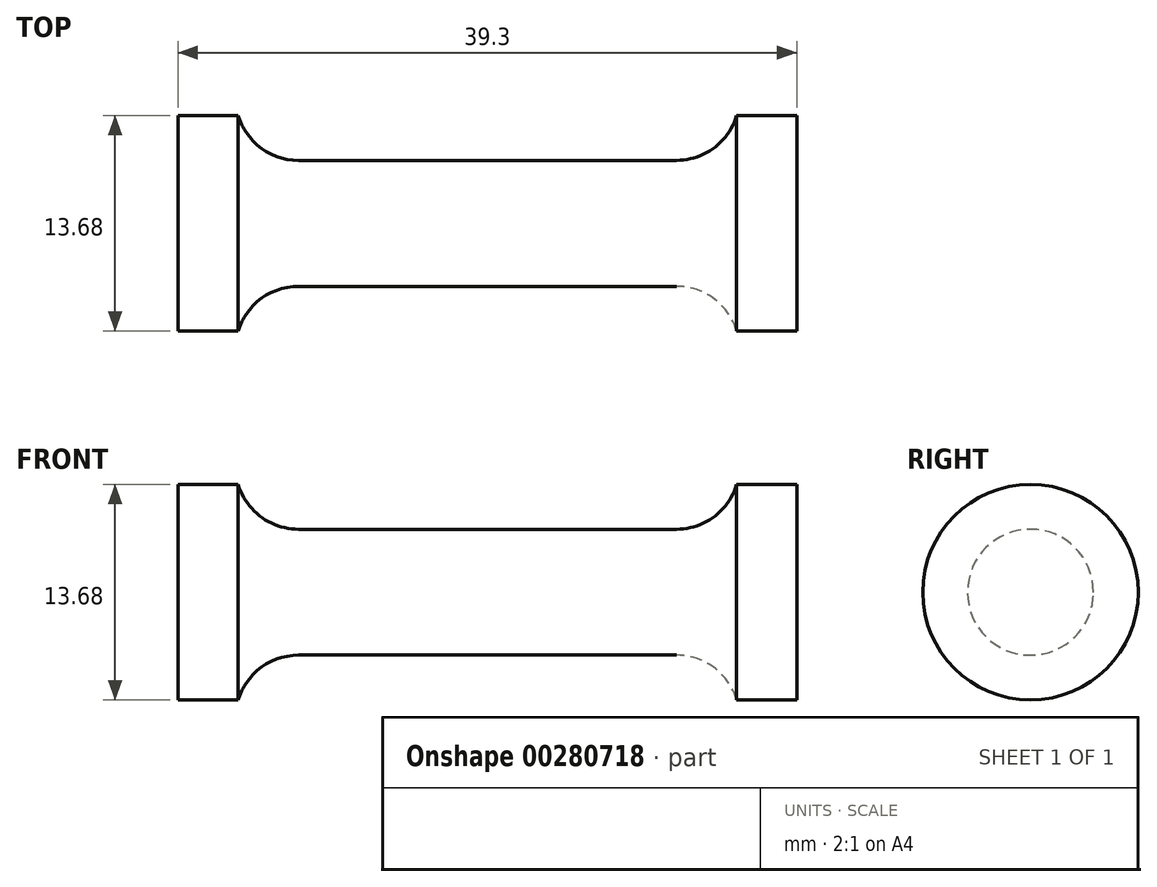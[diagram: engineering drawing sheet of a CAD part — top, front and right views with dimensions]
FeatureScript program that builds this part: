
annotation { "Feature Type Name" : "Feature", "Feature Type Description" : "" }
export const myFeature = defineFeature(function(context is Context, id is Id, definition is map)
    precondition{}
    {
        {
            var Q0;
            Q0=qCreatedBy(makeId("Front.planeOp"),FACE);
            var sketch = newSketch(context, id + "F0", { "sketchPlane" : qUnion([Q0])});
            skLineSegment(sketch, "E0", {"start": v(0, 4) * mm, "end": v(12, 4) * mm});
            skArc(sketch, "E1", {"start": v(12, 4) * mm, "mid": v(14.39, 4.79) * mm, "end": v(15.83, 6.84) * mm});
            skLineSegment(sketch, "E2", {"start": v(15.83, 6.84) * mm, "end": v(19.65, 6.84) * mm});
            skLineSegment(sketch, "E3", {"start": v(19.65, 6.84) * mm, "end": v(19.65, 0) * mm});
            skLineSegment(sketch, "E4.MirrorCS", {"start": v(0, 4) * mm, "end": v(-12, 4) * mm});
            skLineSegment(sketch, "E5.MirrorCS", {"start": v(-19.65, 6.84) * mm, "end": v(-19.65, 0) * mm});
            skLineSegment(sketch, "E6.MirrorCS", {"start": v(-15.83, 6.84) * mm, "end": v(-19.65, 6.84) * mm});
            skArc(sketch, "E7.MirrorCS", {"start": v(-12, 4) * mm, "mid": v(-14.39, 4.79) * mm, "end": v(-15.83, 6.84) * mm});
            skLineSegment(sketch, "E8", {"start": v(-19.65, 0) * mm, "end": v(19.65, 0) * mm});
            skSolve(sketch);
        }
        {
            var Q0;
            Q0 = qSketchRegion(id + "F0", true);
            var Q1;
            Q1=sQuery(id+"F0.wireOp",EDGE,"E8");
            revolve(context, id + "F1", {"entities" : qUnion([Q0]), "axis" : qUnion([Q1]), "revolveType" : RevolveType.FULL});
        }
    });
